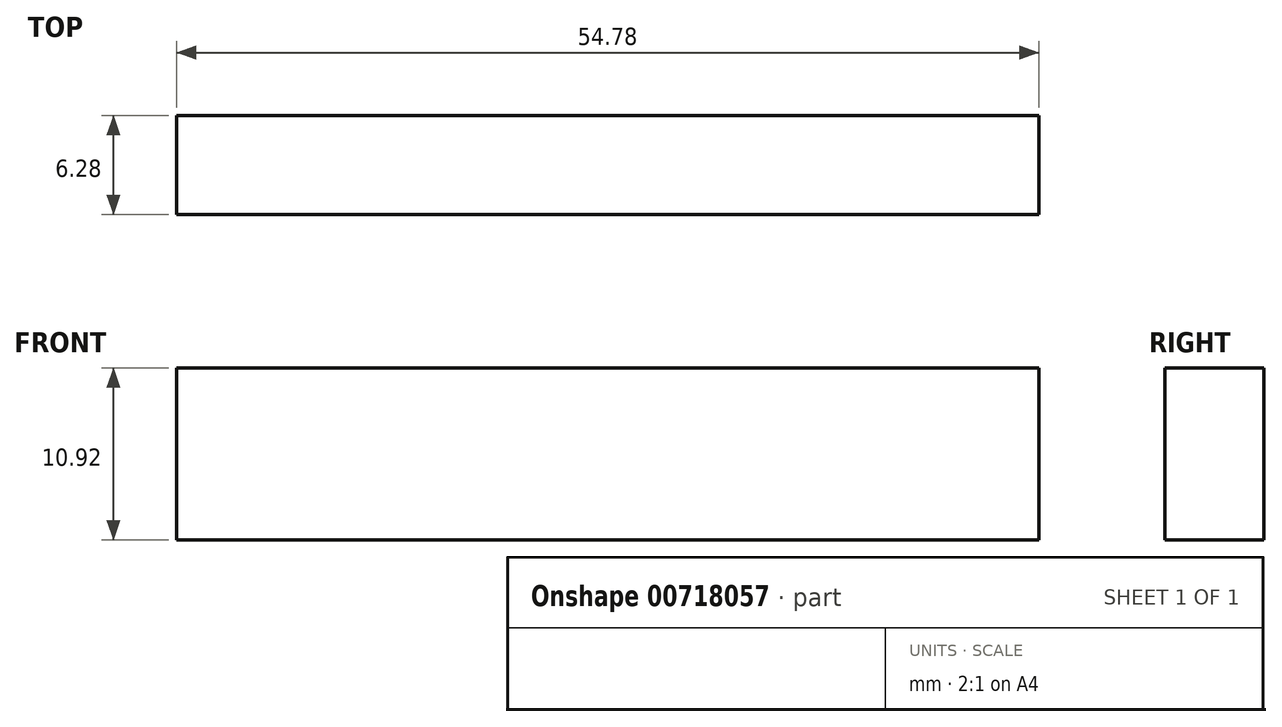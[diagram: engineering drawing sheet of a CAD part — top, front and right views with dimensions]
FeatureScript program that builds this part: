
annotation { "Feature Type Name" : "Feature", "Feature Type Description" : "" }
export const myFeature = defineFeature(function(context is Context, id is Id, definition is map)
    precondition{}
    {
        {
            var Q0;
            Q0=qCreatedBy(makeId("Front.planeOp"),FACE);
            var sketch = newSketch(context, id + "F0", { "sketchPlane" : qUnion([Q0])});
            skLineSegment(sketch, "E0.bottom", {"start": v(0, 0) * mm, "end": v(95.63, 0) * mm});
            skLineSegment(sketch, "E0.top", {"start": v(0, 97.83) * mm, "end": v(95.63, 97.83) * mm});
            skLineSegment(sketch, "E0.left", {"start": v(0, 0) * mm, "end": v(0, 97.83) * mm});
            skLineSegment(sketch, "E0.right", {"start": v(95.63, 0) * mm, "end": v(95.63, 97.83) * mm});
            skLineSegment(sketch, "E1.bottom", {"start": v(0, 97.83) * mm, "end": v(-94.65, 97.83) * mm});
            skLineSegment(sketch, "E1.top", {"start": v(0, -95.54) * mm, "end": v(-94.65, -95.54) * mm});
            skLineSegment(sketch, "E1.left", {"start": v(0, 97.83) * mm, "end": v(0, -95.54) * mm});
            skLineSegment(sketch, "E1.right", {"start": v(-94.65, 97.83) * mm, "end": v(-94.65, -95.54) * mm});
            skLineSegment(sketch, "E2.bottom", {"start": v(0, -95.54) * mm, "end": v(95.63, -95.54) * mm});
            skLineSegment(sketch, "E2.left", {"start": v(0, -95.54) * mm, "end": v(0, 0) * mm});
            skLineSegment(sketch, "E2.right", {"start": v(95.63, -95.54) * mm, "end": v(95.63, 0) * mm});
            skLineSegment(sketch, "E3.bottom", {"start": v(-34.5, 130.58) * mm, "end": v(16.55, 130.58) * mm});
            skLineSegment(sketch, "E3.top", {"start": v(-34.5, -108.24) * mm, "end": v(16.55, -108.24) * mm});
            skLineSegment(sketch, "E3.left", {"start": v(-34.5, 130.58) * mm, "end": v(-34.5, -108.24) * mm});
            skLineSegment(sketch, "E3.right", {"start": v(16.55, 130.58) * mm, "end": v(16.55, -108.24) * mm});
            skLineSegment(sketch, "E4.bottom", {"start": v(16.55, 130.58) * mm, "end": v(149.66, 130.58) * mm});
            skLineSegment(sketch, "E4.top", {"start": v(16.55, -99) * mm, "end": v(149.66, -99) * mm});
            skLineSegment(sketch, "E4.left", {"start": v(16.55, 130.58) * mm, "end": v(16.55, -99) * mm});
            skLineSegment(sketch, "E4.right", {"start": v(149.66, 130.58) * mm, "end": v(149.66, -99) * mm});
            skLineSegment(sketch, "E5.bottom", {"start": v(-34.5, -95.54) * mm, "end": v(-151.3, -95.54) * mm});
            skLineSegment(sketch, "E5.top", {"start": v(-34.5, 120.83) * mm, "end": v(-151.3, 120.83) * mm});
            skLineSegment(sketch, "E5.left", {"start": v(-34.5, -95.54) * mm, "end": v(-34.5, 120.83) * mm});
            skLineSegment(sketch, "E5.right", {"start": v(-151.3, -95.54) * mm, "end": v(-151.3, 120.83) * mm});
            skSolve(sketch);
        }
        {
            var Q0;
            Q0=qSketchRegion(id+"F0",true);
            extrude(context, id + "F1", {"entities" : qUnion([Q0]), "depth" : 25.4 * mm, "offsetDistance" : 25.4 * mm});
        }
        {
            var Q0;
            Q0=makeQuery(id+"F1.opExtrude","CAP_FACE",FACE,{"disambiguationData":[OSD([sQuery(id+"F0.wireOp",EDGE,"E0.top"),sQuery(id+"F0.wireOp",EDGE,"E0.right"),sQuery(id+"F0.wireOp",EDGE,"E1.left"),sQuery(id+"F0.wireOp",EDGE,"E2.bottom"),sQuery(id+"F0.wireOp",EDGE,"E2.left"),sQuery(id+"F0.wireOp",EDGE,"E2.right"),sQuery(id+"F0.wireOp",EDGE,"E3.bottom"),sQuery(id+"F0.wireOp",EDGE,"E3.top"),sQuery(id+"F0.wireOp",EDGE,"E3.left"),sQuery(id+"F0.wireOp",EDGE,"E3.right"),sQuery(id+"F0.wireOp",EDGE,"E4.bottom"),sQuery(id+"F0.wireOp",EDGE,"E4.top"),sQuery(id+"F0.wireOp",EDGE,"E4.right"),sQuery(id+"F0.wireOp",EDGE,"E5.bottom"),sQuery(id+"F0.wireOp",EDGE,"E5.top"),sQuery(id+"F0.wireOp",EDGE,"E5.right")])],"isStart":true});
            var sketch = newSketch(context, id + "F2", { "sketchPlane" : qUnion([Q0])});
            skLineSegment(sketch, "E6.bottom", {"start": v(-95.63, 108.88) * mm, "end": v(291.77, 108.88) * mm});
            skLineSegment(sketch, "E6.top", {"start": v(-95.63, -277) * mm, "end": v(291.77, -277) * mm});
            skLineSegment(sketch, "E6.left", {"start": v(-95.63, 108.88) * mm, "end": v(-95.63, -277) * mm});
            skLineSegment(sketch, "E6.right", {"start": v(291.77, 108.88) * mm, "end": v(291.77, -277) * mm});
            skPoint(sketch, "E6.middle", {"position": v(98.07, -84.06) * mm});
            skSolve(sketch);
        }
        {
            var Q0;
            {var subQ13=makeQuery(id+"F1.opExtrude","CAP_EDGE",EDGE,{"disambiguationData":[OSD([sQuery(id+"F0.wireOp",EDGE,"E0.top")])],"isStart":true});Q0=makeQuery(id+"F2.imprint","IMPRINT",FACE,{"disambiguationData":[TD([[makeQuery(id+"F2.imprint","IMPRINT",EDGE,{"derivedFrom":subQ13}),-1.0]])]});}
            var Q1;
            {var subQ1=makeQuery(id+"F1.opExtrude","CAP_EDGE",EDGE,{"disambiguationData":[OSD([sQuery(id+"F0.wireOp",EDGE,"E0.top")])],"isStart":true});Q1=makeQuery(id+"F2.imprint","IMPRINT",FACE,{"disambiguationData":[TD([[makeQuery(id+"F2.imprint","IMPRINT",EDGE,{"derivedFrom":subQ1}),1.0]])]});}
            extrude(context, id + "F3", {"entities" : qUnion([Q0, Q1]), "operationType" : NewBodyOperationType.ADD, "oppositeDirection" : true, "depth" : 346.17 * mm, "offsetDistance" : 25.4 * mm});
        }
        {
            var Q0;
            {var subQ0=sQuery(id+"F0.wireOp",EDGE,"E5.right");var subQ1=sQuery(id+"F0.wireOp",EDGE,"E5.bottom");var subQ2=sQuery(id+"F0.wireOp",EDGE,"E4.top");var subQ3=sQuery(id+"F0.wireOp",EDGE,"E3.right");var subQ4=sQuery(id+"F0.wireOp",EDGE,"E3.left");var subQ5=sQuery(id+"F0.wireOp",EDGE,"E3.top");Q0=makeQuery(id+"F3.boolean.opBoolean","MERGE",FACE,{"derivedFrom":[makeQuery(id+"F1.opExtrude","CAP_FACE",FACE,{"disambiguationData":[OSD([sQuery(id+"F0.wireOp",EDGE,"E0.top"),sQuery(id+"F0.wireOp",EDGE,"E0.right"),sQuery(id+"F0.wireOp",EDGE,"E1.left"),sQuery(id+"F0.wireOp",EDGE,"E2.bottom"),sQuery(id+"F0.wireOp",EDGE,"E2.left"),sQuery(id+"F0.wireOp",EDGE,"E2.right"),sQuery(id+"F0.wireOp",EDGE,"E3.bottom"),subQ5,subQ4,subQ3,sQuery(id+"F0.wireOp",EDGE,"E4.bottom"),subQ2,sQuery(id+"F0.wireOp",EDGE,"E4.right"),subQ1,sQuery(id+"F0.wireOp",EDGE,"E5.top"),subQ0])],"isStart":true}),makeQuery(id+"F3.opExtrude","CAP_FACE",FACE,{"disambiguationData":[OSD([subQ5,subQ4,subQ3,subQ2,subQ1,subQ0,sQuery(id+"F2.wireOp",EDGE,"E6.bottom"),sQuery(id+"F2.wireOp",EDGE,"E6.left")])],"isStart":true})]});}
            var sketch = newSketch(context, id + "F4", { "sketchPlane" : qUnion([Q0])});
            skLineSegment(sketch, "E7.bottom", {"start": v(-77.36, 89.2) * mm, "end": v(78.88, 89.2) * mm});
            skLineSegment(sketch, "E7.top", {"start": v(-77.36, -67.08) * mm, "end": v(78.88, -67.08) * mm});
            skLineSegment(sketch, "E7.left", {"start": v(-77.36, 89.2) * mm, "end": v(-77.36, -67.08) * mm});
            skLineSegment(sketch, "E7.right", {"start": v(78.88, 89.2) * mm, "end": v(78.88, -67.08) * mm});
            skLineSegment(sketch, "E8.bottom", {"start": v(-113.4, 15.53) * mm, "end": v(-77.36, 15.53) * mm});
            skLineSegment(sketch, "E8.top", {"start": v(-113.4, 43.9) * mm, "end": v(-77.36, 43.9) * mm});
            skLineSegment(sketch, "E8.left", {"start": v(-113.4, 15.53) * mm, "end": v(-113.4, 43.9) * mm});
            skLineSegment(sketch, "E8.right", {"start": v(-77.36, 15.53) * mm, "end": v(-77.36, 43.9) * mm});
            skLineSegment(sketch, "E9.top", {"start": v(-113.4, -26.5) * mm, "end": v(-77.36, -26.5) * mm});
            skLineSegment(sketch, "E9.left", {"start": v(-113.4, 15.53) * mm, "end": v(-113.4, -26.5) * mm});
            skLineSegment(sketch, "E9.right", {"start": v(-77.36, 15.53) * mm, "end": v(-77.36, -26.5) * mm});
            skLineSegment(sketch, "E10.top", {"start": v(-113.4, -67.08) * mm, "end": v(-77.36, -67.08) * mm});
            skLineSegment(sketch, "E10.left", {"start": v(-113.4, -26.5) * mm, "end": v(-113.4, -67.08) * mm});
            skLineSegment(sketch, "E10.right", {"start": v(-77.36, -26.5) * mm, "end": v(-77.36, -67.08) * mm});
            skLineSegment(sketch, "E11.top", {"start": v(-113.4, 89.2) * mm, "end": v(-77.36, 89.2) * mm});
            skLineSegment(sketch, "E11.left", {"start": v(-113.4, 43.9) * mm, "end": v(-113.4, 89.2) * mm});
            skLineSegment(sketch, "E11.right", {"start": v(-77.36, 43.9) * mm, "end": v(-77.36, 89.2) * mm});
            skSolve(sketch);
        }
        {
            var Q0;
            Q0=qSketchRegion(id+"F4",true);
            extrude(context, id + "F5", {"entities" : qUnion([Q0]), "operationType" : NewBodyOperationType.ADD, "depth" : 25.4 * mm, "offsetDistance" : 25.4 * mm});
        }
        {
            var Q0;
            Q0=makeQuery(id+"F5.opExtrude","CAP_FACE",FACE,{"disambiguationData":[OSD([sQuery(id+"F4.wireOp",EDGE,"E7.bottom"),sQuery(id+"F4.wireOp",EDGE,"E7.top"),sQuery(id+"F4.wireOp",EDGE,"E7.right"),sQuery(id+"F4.wireOp",EDGE,"E8.left"),sQuery(id+"F4.wireOp",EDGE,"E9.left"),sQuery(id+"F4.wireOp",EDGE,"E10.top"),sQuery(id+"F4.wireOp",EDGE,"E10.left"),sQuery(id+"F4.wireOp",EDGE,"E11.top"),sQuery(id+"F4.wireOp",EDGE,"E11.left")])],"isStart":false});
            var sketch = newSketch(context, id + "F6", { "sketchPlane" : qUnion([Q0])});
            skLineSegment(sketch, "E12.bottom", {"start": v(-94.88, 89.2) * mm, "end": v(78.88, 89.2) * mm});
            skLineSegment(sketch, "E12.top", {"start": v(-94.88, -67.08) * mm, "end": v(78.88, -67.08) * mm});
            skLineSegment(sketch, "E12.left", {"start": v(-94.88, 89.2) * mm, "end": v(-94.88, -67.08) * mm});
            skLineSegment(sketch, "E12.right", {"start": v(78.88, 89.2) * mm, "end": v(78.88, -67.08) * mm});
            skSolve(sketch);
        }
        {
            var Q0;
            Q0=qSketchRegion(id+"F6",true);
            extrude(context, id + "F7", {"entities" : qUnion([Q0]), "operationType" : NewBodyOperationType.ADD, "depth" : 25.4 * mm, "offsetDistance" : 25.4 * mm});
        }
        {
            var Q0;
            Q0=makeQuery(id+"F7.opExtrude","SWEPT_FACE",FACE,{"disambiguationData":[OSD([sQuery(id+"F6.wireOp",EDGE,"E12.left")])]});
            var sketch = newSketch(context, id + "F8", { "sketchPlane" : qUnion([Q0])});
            skLineSegment(sketch, "E13.bottom", {"start": v(50.8, -67.08) * mm, "end": v(186.61, -67.08) * mm});
            skLineSegment(sketch, "E13.top", {"start": v(50.8, 89.35) * mm, "end": v(186.61, 89.35) * mm});
            skLineSegment(sketch, "E13.left", {"start": v(50.8, -67.08) * mm, "end": v(50.8, 89.35) * mm});
            skLineSegment(sketch, "E13.right", {"start": v(186.61, -67.08) * mm, "end": v(186.61, 89.35) * mm});
            skLineSegment(sketch, "E14.bottom", {"start": v(186.61, -67.08) * mm, "end": v(74.87, -67.08) * mm});
            skLineSegment(sketch, "E14.top", {"start": v(186.61, -85.28) * mm, "end": v(74.87, -85.28) * mm});
            skLineSegment(sketch, "E14.left", {"start": v(186.61, -67.08) * mm, "end": v(186.61, -85.28) * mm});
            skLineSegment(sketch, "E14.right", {"start": v(74.87, -67.08) * mm, "end": v(74.87, -85.28) * mm});
            skLineSegment(sketch, "E15.bottom", {"start": v(186.61, -67.08) * mm, "end": v(50.8, -67.08) * mm});
            skLineSegment(sketch, "E15.top", {"start": v(186.61, 89.35) * mm, "end": v(50.8, 89.35) * mm});
            skLineSegment(sketch, "E16.bottom", {"start": v(75.5, 70.37) * mm, "end": v(112.96, 70.37) * mm});
            skLineSegment(sketch, "E16.top", {"start": v(75.5, 100.12) * mm, "end": v(112.96, 100.12) * mm});
            skLineSegment(sketch, "E16.left", {"start": v(75.5, 70.37) * mm, "end": v(75.5, 100.12) * mm});
            skLineSegment(sketch, "E16.right", {"start": v(112.96, 70.37) * mm, "end": v(112.96, 100.12) * mm});
            skLineSegment(sketch, "E17.bottom", {"start": v(75.5, 100.12) * mm, "end": v(50.8, 100.12) * mm});
            skLineSegment(sketch, "E17.top", {"start": v(75.5, 89.2) * mm, "end": v(50.8, 89.2) * mm});
            skLineSegment(sketch, "E17.left", {"start": v(75.5, 100.12) * mm, "end": v(75.5, 89.2) * mm});
            skLineSegment(sketch, "E17.right", {"start": v(50.8, 100.12) * mm, "end": v(50.8, 89.2) * mm});
            skPoint(sketch, "E18.oppositeSnap0", {"position": v(38.1, 89.2) * mm});
            skLineSegment(sketch, "E18.bottom", {"start": v(50.8, 100.12) * mm, "end": v(-6.28, 100.12) * mm});
            skLineSegment(sketch, "E18.top", {"start": v(50.8, 89.2) * mm, "end": v(-6.28, 89.2) * mm});
            skLineSegment(sketch, "E18.right", {"start": v(-6.28, 100.12) * mm, "end": v(-6.28, 89.2) * mm});
            skSolve(sketch);
        }
        {
            var Q0;
            Q0=qSketchRegion(id+"F8",true);
            extrude(context, id + "F9", {"entities" : qUnion([Q0]), "operationType" : NewBodyOperationType.INTERSECT, "depth" : 3015.54 * mm, "offsetDistance" : 25.4 * mm});
        }
    });
